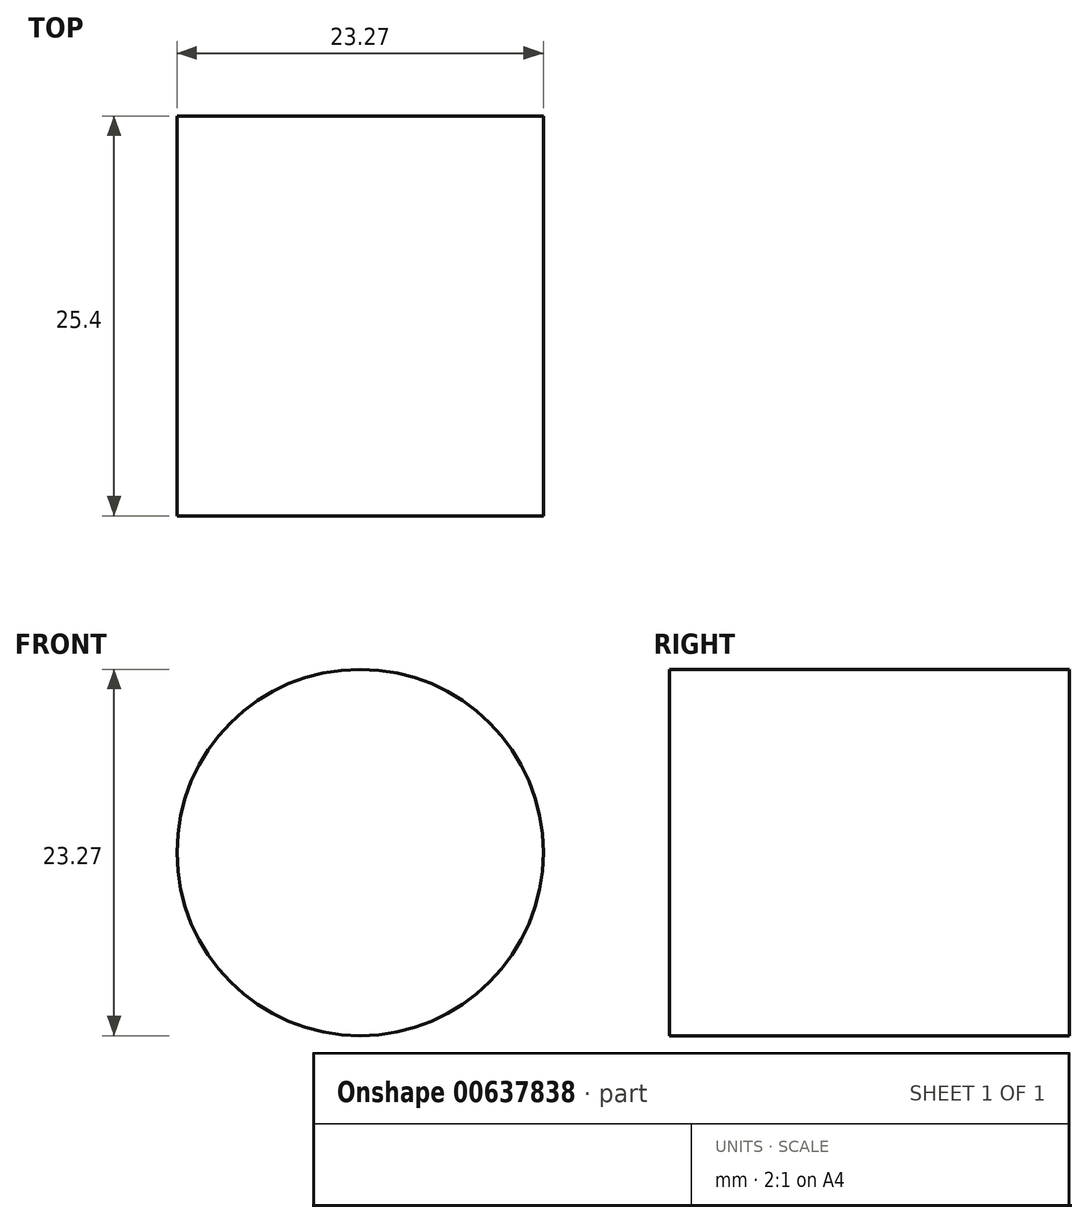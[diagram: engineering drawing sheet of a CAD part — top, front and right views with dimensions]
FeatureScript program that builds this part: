
annotation { "Feature Type Name" : "Feature", "Feature Type Description" : "" }
export const myFeature = defineFeature(function(context is Context, id is Id, definition is map)
    precondition{}
    {
        {
            var Q0;
            Q0=qCreatedBy(makeId("Front.planeOp"),FACE);
            var sketch = newSketch(context, id + "F0", { "sketchPlane" : qUnion([Q0])});
            skCircle(sketch, "E0", {"center": v(-60.82, 58.53) * mm, "radius": 11.63 * mm});
            skSolve(sketch);
        }
        {
            var Q0;
            Q0 = qSketchRegion(id + "F0", true);
            extrude(context, id + "F1", {"entities" : qUnion([Q0]), "depth" : 25.4 * mm, "offsetDistance" : 25.4 * mm});
        }
    });
